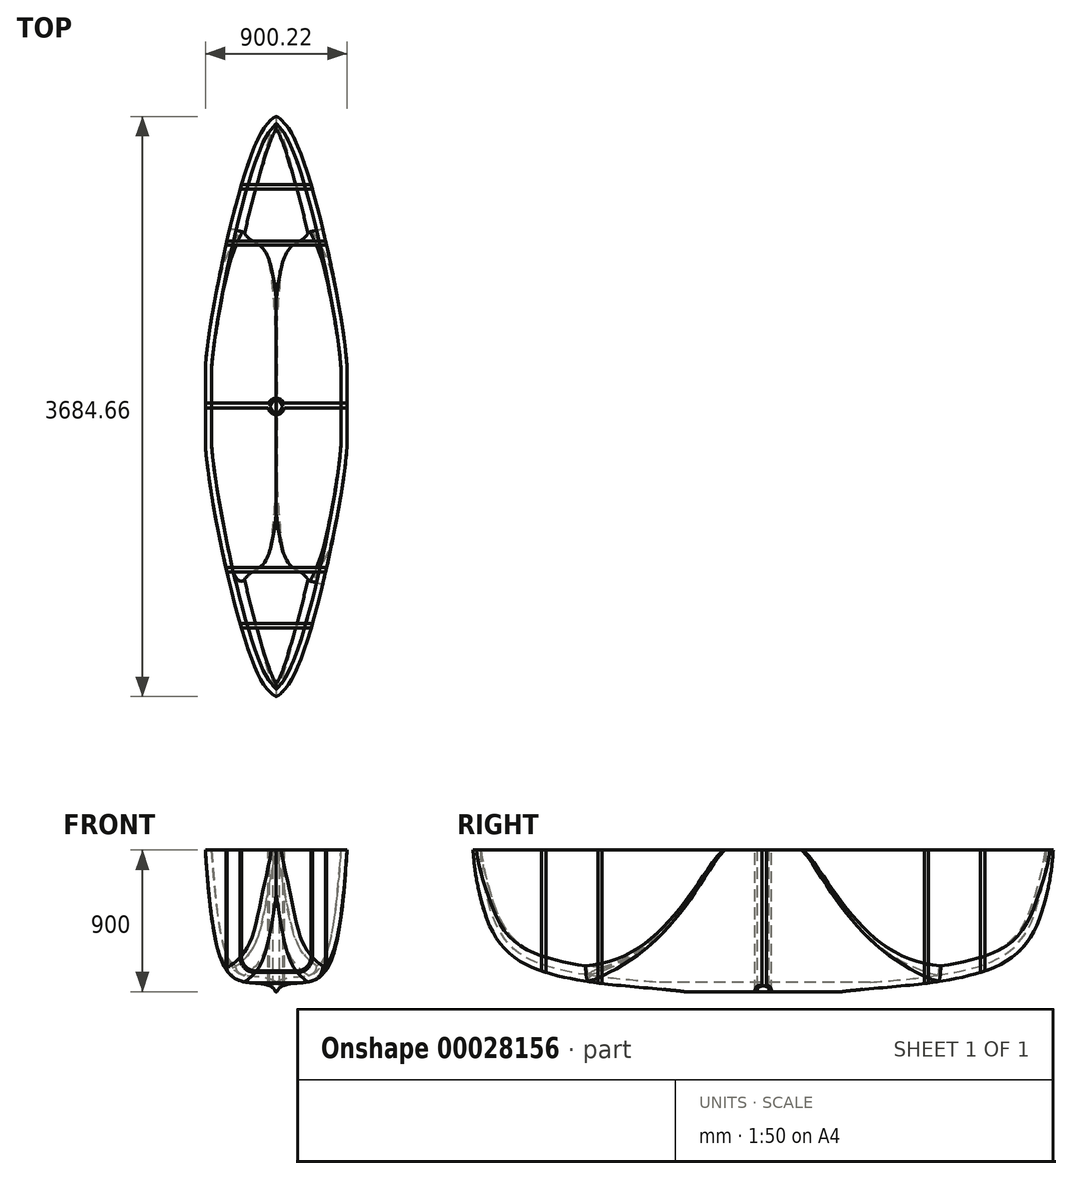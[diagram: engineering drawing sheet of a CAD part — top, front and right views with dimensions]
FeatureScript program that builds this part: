
annotation { "Feature Type Name" : "Feature", "Feature Type Description" : "" }
export const myFeature = defineFeature(function(context is Context, id is Id, definition is map)
    precondition{}
    {
        {
            var Q0;
            Q0=qCreatedBy(makeId("Front.planeOp"),FACE);
            var sketch = newSketch(context, id + "F0", { "sketchPlane" : qUnion([Q0])});
            skLineSegment(sketch, "E0.rect.bottom", {"start": v(450, -450) * mm, "end": v(-450, -450) * mm});
            skLineSegment(sketch, "E0.rect.top", {"start": v(450, 450) * mm, "end": v(-450, 450) * mm});
            skLineSegment(sketch, "E0.rect.left", {"start": v(450, -450) * mm, "end": v(450, 450) * mm});
            skLineSegment(sketch, "E0.rect.right", {"start": v(-450, -450) * mm, "end": v(-450, 450) * mm});
            skPoint(sketch, "E0.rect.middle", {"position": v(0, 0) * mm});
            skSolve(sketch);
        }
        {
            var Q0;
            Q0 = qSketchRegion(id + "F0", true);
            extrude(context, id + "F1", {"entities" : qUnion([Q0]), "endBound" : BoundingType.SYMMETRIC, "depth" : 3700 * mm});
        }
        {
            var Q0;
            Q0=makeQuery(id+"F1.opExtrude","CAP_FACE",FACE,{"disambiguationData":[OSD([sQuery(id+"F0.wireOp",EDGE,"E0.rect.bottom"),sQuery(id+"F0.wireOp",EDGE,"E0.rect.top"),sQuery(id+"F0.wireOp",EDGE,"E0.rect.left"),sQuery(id+"F0.wireOp",EDGE,"E0.rect.right")])],"isStart":false});
            var sketch = newSketch(context, id + "F2", { "sketchPlane" : qUnion([Q0])});
            skLineSegment(sketch, "E1", {"start": v(0, -450) * mm, "end": v(0, 450) * mm, "construction": true});
            skLineSegment(sketch, "E2", {"start": v(0, -450) * mm, "end": v(5, -450) * mm});
            skFitSpline(sketch, "E3", {"points": [v(5, -450) * mm, v(227.43, -381.86) * mm, v(386.95, -116.91) * mm, v(450, 450) * mm], "startDerivative": vector(294.58, 786.1) * mm, "endDerivative": vector(57.57, 897.48) * mm});
            skLineSegment(sketch, "E4.MirrorCS", {"start": v(0, -450) * mm, "end": v(-5, -450) * mm});
            skFitSpline(sketch, "E5.MirrorCS", {"points": [v(-5, -450) * mm, v(-227.43, -381.86) * mm, v(-386.95, -116.91) * mm, v(-450, 450) * mm], "startDerivative": vector(-294.58, 786.1) * mm, "endDerivative": vector(-57.57, 897.48) * mm});
            skSolve(sketch);
        }
        {
            var Q0;
            Q0=makeQuery(id+"F1.opExtrude","SWEPT_FACE",FACE,{"disambiguationData":[OSD([sQuery(id+"F0.wireOp",EDGE,"E0.rect.right")])]});
            var sketch = newSketch(context, id + "F3", { "sketchPlane" : qUnion([Q0])});
            skLineSegment(sketch, "E6", {"start": v(0, -450) * mm, "end": v(500, -450) * mm});
            skLineSegment(sketch, "E7", {"start": v(0, -450) * mm, "end": v(0, 450) * mm, "construction": true});
            skFitSpline(sketch, "E8", {"points": [v(500, -450) * mm, v(1533.69, -262.8) * mm, v(1795.23, 146) * mm, v(1850, 450) * mm], "startDerivative": vector(1866.26, 245.74) * mm, "endDerivative": vector(116.04, 1077.86) * mm});
            skLineSegment(sketch, "E9.MirrorCS", {"start": v(0, -450) * mm, "end": v(-500, -450) * mm});
            skFitSpline(sketch, "E10.MirrorCS", {"points": [v(-500, -450) * mm, v(-1533.69, -262.8) * mm, v(-1795.23, 146) * mm, v(-1850, 450) * mm], "startDerivative": vector(-1866.26, 245.74) * mm, "endDerivative": vector(-116.04, 1077.86) * mm});
            skSolve(sketch);
        }
        {
            var Q0;
            {var subQ2=sQuery(id+"F3.wireOp",EDGE,"E10.MirrorCS");Q0=makeQuery(id+"F3.imprint","IMPRINT",FACE,{"disambiguationData":[TD([[makeQuery(id+"F3.imprint","IMPRINT",EDGE,{"derivedFrom":subQ2}),1.0]])]});}
            var Q1;
            {var subQ2=sQuery(id+"F3.wireOp",EDGE,"E8");Q1=makeQuery(id+"F3.imprint","IMPRINT",FACE,{"disambiguationData":[TD([[makeQuery(id+"F3.imprint","IMPRINT",EDGE,{"derivedFrom":subQ2}),-1.0]])]});}
            extrude(context, id + "F4", {"entities" : qUnion([Q0, Q1]), "operationType" : NewBodyOperationType.REMOVE, "endBound" : BoundingType.THROUGH_ALL, "oppositeDirection" : true, "depth" : 25 * mm});
        }
        {
            var Q0;
            {var subQ1=sQuery(id+"F2.wireOp",EDGE,"E3");Q0=makeQuery(id+"F2.imprint","IMPRINT",FACE,{"disambiguationData":[TD([[makeQuery(id+"F2.imprint","IMPRINT",EDGE,{"derivedFrom":subQ1}),-1.0]])]});}
            var Q1;
            {var subQ1=sQuery(id+"F2.wireOp",EDGE,"E5.MirrorCS");Q1=makeQuery(id+"F2.imprint","IMPRINT",FACE,{"disambiguationData":[TD([[makeQuery(id+"F2.imprint","IMPRINT",EDGE,{"derivedFrom":subQ1}),1.0]])]});}
            extrude(context, id + "F5", {"entities" : qUnion([Q0, Q1]), "operationType" : NewBodyOperationType.REMOVE, "endBound" : BoundingType.THROUGH_ALL, "oppositeDirection" : true, "depth" : 25 * mm});
        }
        {
            var Q0;
            Q0=makeQuery(id+"F1.opExtrude","SWEPT_FACE",FACE,{"disambiguationData":[OSD([sQuery(id+"F0.wireOp",EDGE,"E0.rect.top")])]});
            var sketch = newSketch(context, id + "F6", { "sketchPlane" : qUnion([Q0])});
            skLineSegment(sketch, "E11", {"start": v(-450, 0) * mm, "end": v(450, 0) * mm, "construction": true});
            skLineSegment(sketch, "E12", {"start": v(-450, 0) * mm, "end": v(-450, 250) * mm});
            skLineSegment(sketch, "E13", {"start": v(0, 1850) * mm, "end": v(0, -1850) * mm, "construction": true});
            skFitSpline(sketch, "E14", {"points": [v(-450, 250) * mm, v(-293.35, 1137.47) * mm, v(-112.56, 1707.62) * mm, v(0, 1850) * mm], "startDerivative": vector(77.55, 1314.78) * mm, "endDerivative": vector(838.8, 705.86) * mm});
            skFitSpline(sketch, "E15.MirrorCS", {"points": [v(-450, -250) * mm, v(-293.35, -1137.47) * mm, v(-112.56, -1707.62) * mm, v(0, -1850) * mm], "startDerivative": vector(77.55, -1314.78) * mm, "endDerivative": vector(838.8, -705.86) * mm});
            skLineSegment(sketch, "E16.MirrorCS", {"start": v(-450, 0) * mm, "end": v(-450, -250) * mm});
            skFitSpline(sketch, "E17.MirrorCS", {"points": [v(450, 250) * mm, v(293.35, 1137.47) * mm, v(112.56, 1707.62) * mm, v(0, 1850) * mm], "startDerivative": vector(-77.55, 1314.78) * mm, "endDerivative": vector(-838.8, 705.86) * mm});
            skLineSegment(sketch, "E18.MirrorCS", {"start": v(450, 0) * mm, "end": v(450, 250) * mm});
            skLineSegment(sketch, "E19.MirrorCS", {"start": v(450, 0) * mm, "end": v(450, -250) * mm});
            skFitSpline(sketch, "E20.MirrorCS", {"points": [v(450, -250) * mm, v(293.35, -1137.47) * mm, v(112.56, -1707.62) * mm, v(0, -1850) * mm], "startDerivative": vector(-77.55, -1314.78) * mm, "endDerivative": vector(-838.8, -705.86) * mm});
            skSolve(sketch);
        }
        {
            var Q0;
            {var subQ3=sQuery(id+"F6.wireOp",EDGE,"E14");Q0=makeQuery(id+"F6.imprint","IMPRINT",FACE,{"disambiguationData":[TD([[makeQuery(id+"F6.imprint","IMPRINT",EDGE,{"derivedFrom":subQ3}),1.0]])]});}
            var Q1;
            {var subQ3=sQuery(id+"F6.wireOp",EDGE,"E17.MirrorCS");Q1=makeQuery(id+"F6.imprint","IMPRINT",FACE,{"disambiguationData":[TD([[makeQuery(id+"F6.imprint","IMPRINT",EDGE,{"derivedFrom":subQ3}),-1.0]])]});}
            var Q2;
            {var subQ3=sQuery(id+"F6.wireOp",EDGE,"E20.MirrorCS");Q2=makeQuery(id+"F6.imprint","IMPRINT",FACE,{"disambiguationData":[TD([[makeQuery(id+"F6.imprint","IMPRINT",EDGE,{"derivedFrom":subQ3}),1.0]])]});}
            var Q3;
            {var subQ3=sQuery(id+"F6.wireOp",EDGE,"E15.MirrorCS");Q3=makeQuery(id+"F6.imprint","IMPRINT",FACE,{"disambiguationData":[TD([[makeQuery(id+"F6.imprint","IMPRINT",EDGE,{"derivedFrom":subQ3}),-1.0]])]});}
            extrude(context, id + "F7", {"entities" : qUnion([Q0, Q1, Q2, Q3]), "operationType" : NewBodyOperationType.REMOVE, "endBound" : BoundingType.THROUGH_ALL, "oppositeDirection" : true, "depth" : 25 * mm});
        }
        {
            var Q0;
            Q0=makeQuery(id+"F7.boolean.opBoolean","INTERSECT",EDGE,{"derivedFrom":[makeQuery(id+"F5.boolean.opBoolean","COPY",FACE,{"derivedFrom":makeQuery(id+"F5.opExtrude","SWEPT_FACE",FACE,{"disambiguationData":[OSD([sQuery(id+"F2.wireOp",EDGE,"E5.MirrorCS")])]})}),makeQuery(id+"F7.opExtrude","SWEPT_FACE",FACE,{"disambiguationData":[OSD([sQuery(id+"F6.wireOp",EDGE,"E14")])]})]});
            var Q1;
            Q1=makeQuery(id+"F7.boolean.opBoolean","INTERSECT",EDGE,{"derivedFrom":[makeQuery(id+"F4.boolean.opBoolean","COPY",FACE,{"derivedFrom":makeQuery(id+"F4.opExtrude","SWEPT_FACE",FACE,{"disambiguationData":[OSD([sQuery(id+"F3.wireOp",EDGE,"E10.MirrorCS")])]})}),makeQuery(id+"F7.opExtrude","SWEPT_FACE",FACE,{"disambiguationData":[OSD([sQuery(id+"F6.wireOp",EDGE,"E14")])]})]});
            var Q2;
            Q2=makeQuery(id+"F7.boolean.opBoolean","INTERSECT",EDGE,{"derivedFrom":[makeQuery(id+"F4.boolean.opBoolean","COPY",FACE,{"derivedFrom":makeQuery(id+"F4.opExtrude","SWEPT_FACE",FACE,{"disambiguationData":[OSD([sQuery(id+"F3.wireOp",EDGE,"E8")])]})}),makeQuery(id+"F7.opExtrude","SWEPT_FACE",FACE,{"disambiguationData":[OSD([sQuery(id+"F6.wireOp",EDGE,"E15.MirrorCS")])]})]});
            var Q3;
            Q3=makeQuery(id+"F7.boolean.opBoolean","INTERSECT",EDGE,{"derivedFrom":[makeQuery(id+"F4.boolean.opBoolean","COPY",FACE,{"derivedFrom":makeQuery(id+"F4.opExtrude","SWEPT_FACE",FACE,{"disambiguationData":[OSD([sQuery(id+"F3.wireOp",EDGE,"E8")])]})}),makeQuery(id+"F7.opExtrude","SWEPT_FACE",FACE,{"disambiguationData":[OSD([sQuery(id+"F6.wireOp",EDGE,"E20.MirrorCS")])]})]});
            var Q4;
            Q4=makeQuery(id+"F7.boolean.opBoolean","INTERSECT",EDGE,{"derivedFrom":[makeQuery(id+"F5.boolean.opBoolean","COPY",FACE,{"derivedFrom":makeQuery(id+"F5.opExtrude","SWEPT_FACE",FACE,{"disambiguationData":[OSD([sQuery(id+"F2.wireOp",EDGE,"E3")])]})}),makeQuery(id+"F7.opExtrude","SWEPT_FACE",FACE,{"disambiguationData":[OSD([sQuery(id+"F6.wireOp",EDGE,"E20.MirrorCS")])]})]});
            var Q5;
            Q5=makeQuery(id+"F7.boolean.opBoolean","INTERSECT",EDGE,{"derivedFrom":[makeQuery(id+"F5.boolean.opBoolean","COPY",FACE,{"derivedFrom":makeQuery(id+"F5.opExtrude","SWEPT_FACE",FACE,{"disambiguationData":[OSD([sQuery(id+"F2.wireOp",EDGE,"E3")])]})}),makeQuery(id+"F7.opExtrude","SWEPT_FACE",FACE,{"disambiguationData":[OSD([sQuery(id+"F6.wireOp",EDGE,"E17.MirrorCS")])]})]});
            var Q6;
            Q6=makeQuery(id+"F7.boolean.opBoolean","INTERSECT",EDGE,{"derivedFrom":[makeQuery(id+"F4.boolean.opBoolean","COPY",FACE,{"derivedFrom":makeQuery(id+"F4.opExtrude","SWEPT_FACE",FACE,{"disambiguationData":[OSD([sQuery(id+"F3.wireOp",EDGE,"E10.MirrorCS")])]})}),makeQuery(id+"F7.opExtrude","SWEPT_FACE",FACE,{"disambiguationData":[OSD([sQuery(id+"F6.wireOp",EDGE,"E17.MirrorCS")])]})]});
            fillet(context, id + "F8", {"entities" : qUnion([Q0, Q1, Q2, Q3, Q4, Q5, Q6]), "radius" : 100 * mm, "tangentPropagation" : true, "allowEdgeOverflow" : false});
        }
        {
            var Q0;
            Q0=makeQuery(id+"F1.opExtrude","SWEPT_FACE",FACE,{"disambiguationData":[OSD([sQuery(id+"F0.wireOp",EDGE,"E0.rect.top")])]});
            var sketch = newSketch(context, id + "F9", { "sketchPlane" : qUnion([Q0])});
            skCircle(sketch, "E21.cCircle", {"center": v(0, 0) * mm, "radius": 43.3 * mm, "construction": true});
            skLineSegment(sketch, "E21.0", {"start": v(21.65, -37.5) * mm, "end": v(-21.65, -37.5) * mm});
            skLineSegment(sketch, "E21.1", {"start": v(-21.65, -37.5) * mm, "end": v(-43.3, 0) * mm});
            skLineSegment(sketch, "E21.2", {"start": v(-43.3, 0) * mm, "end": v(-21.65, 37.5) * mm});
            skLineSegment(sketch, "E21.3", {"start": v(-21.65, 37.5) * mm, "end": v(21.65, 37.5) * mm});
            skLineSegment(sketch, "E21.4", {"start": v(21.65, 37.5) * mm, "end": v(43.3, 0) * mm});
            skLineSegment(sketch, "E21.5", {"start": v(43.3, 0) * mm, "end": v(21.65, -37.5) * mm});
            skCircle(sketch, "E22", {"center": v(0, 0) * mm, "radius": 52.5 * mm});
            skLineSegment(sketch, "E23", {"start": v(-48.16, 20.9) * mm, "end": v(-450, 20.9) * mm});
            skLineSegment(sketch, "E24", {"start": v(-450, 20.9) * mm, "end": v(-450, -9.1) * mm});
            skLineSegment(sketch, "E25", {"start": v(-450, -9.1) * mm, "end": v(-51.7, -9.1) * mm});
            skLineSegment(sketch, "E26", {"start": v(48.16, 20.9) * mm, "end": v(450, 20.9) * mm});
            skLineSegment(sketch, "E27", {"start": v(51.7, -9.1) * mm, "end": v(450, -9.1) * mm});
            skLineSegment(sketch, "E28", {"start": v(0, 0) * mm, "end": v(450, 0) * mm, "construction": true});
            skLineSegment(sketch, "E29", {"start": v(0, 0) * mm, "end": v(-450, 0) * mm, "construction": true});
            skLineSegment(sketch, "E30", {"start": v(-313.93, 1050.18) * mm, "end": v(313.93, 1050.18) * mm});
            skLineSegment(sketch, "E31", {"start": v(313.93, 1050.18) * mm, "end": v(319.82, 1024.35) * mm});
            skLineSegment(sketch, "E32", {"start": v(319.82, 1024.35) * mm, "end": v(-319.82, 1024.35) * mm});
            skLineSegment(sketch, "E33.MirrorCS", {"start": v(319.82, -1024.35) * mm, "end": v(-319.82, -1024.35) * mm});
            skLineSegment(sketch, "E34.MirrorCS", {"start": v(-313.93, -1050.18) * mm, "end": v(313.93, -1050.18) * mm});
            skLineSegment(sketch, "E35", {"start": v(-221.23, 1407.5) * mm, "end": v(221.23, 1407.5) * mm});
            skLineSegment(sketch, "E36", {"start": v(221.23, 1407.5) * mm, "end": v(229.37, 1379.73) * mm});
            skLineSegment(sketch, "E37", {"start": v(229.37, 1379.73) * mm, "end": v(-229.37, 1379.73) * mm});
            skLineSegment(sketch, "E38.MirrorCS", {"start": v(229.37, -1379.73) * mm, "end": v(-229.37, -1379.73) * mm});
            skLineSegment(sketch, "E39.MirrorCS", {"start": v(-221.23, -1407.5) * mm, "end": v(221.23, -1407.5) * mm});
            skSolve(sketch);
        }
        {
            var Q0;
            Q0=makeQuery(id+"F9.imprint","IMPRINT",FACE,{"disambiguationData":[TD([[makeQuery(id+"F9.imprint","IMPRINT",EDGE,{"derivedFrom":sQuery(id+"F9.wireOp",EDGE,"E21.0")}),1.0]])]});
            var Q1;
            {var subQ4=sQuery(id+"F9.wireOp",EDGE,"E26");Q1=makeQuery(id+"F9.imprint","IMPRINT",FACE,{"disambiguationData":[TD([[makeQuery(id+"F9.imprint","IMPRINT",EDGE,{"derivedFrom":subQ4}),-1.0]])]});}
            var Q2;
            {var subQ1=sQuery(id+"F9.wireOp",EDGE,"E23");Q2=makeQuery(id+"F9.imprint","IMPRINT",FACE,{"disambiguationData":[TD([[makeQuery(id+"F9.imprint","IMPRINT",EDGE,{"derivedFrom":subQ1}),1.0]])]});}
            var Q3;
            {var subQ2=sQuery(id+"F9.wireOp",EDGE,"E33.MirrorCS");Q3=makeQuery(id+"F9.imprint","IMPRINT",FACE,{"disambiguationData":[TD([[makeQuery(id+"F9.imprint","IMPRINT",EDGE,{"derivedFrom":subQ2}),1.0]])]});}
            var Q4;
            {var subQ2=sQuery(id+"F9.wireOp",EDGE,"E30");Q4=makeQuery(id+"F9.imprint","IMPRINT",FACE,{"disambiguationData":[TD([[makeQuery(id+"F9.imprint","IMPRINT",EDGE,{"derivedFrom":subQ2}),-1.0]])]});}
            var Q5;
            {var subQ2=sQuery(id+"F9.wireOp",EDGE,"E35");Q5=makeQuery(id+"F9.imprint","IMPRINT",FACE,{"disambiguationData":[TD([[makeQuery(id+"F9.imprint","IMPRINT",EDGE,{"derivedFrom":subQ2}),-1.0]])]});}
            var Q6;
            {var subQ2=sQuery(id+"F9.wireOp",EDGE,"E38.MirrorCS");Q6=makeQuery(id+"F9.imprint","IMPRINT",FACE,{"disambiguationData":[TD([[makeQuery(id+"F9.imprint","IMPRINT",EDGE,{"derivedFrom":subQ2}),1.0]])]});}
            extrude(context, id + "F10", {"entities" : qUnion([Q0, Q1, Q2, Q3, Q4, Q5, Q6]), "endBound" : BoundingType.UP_TO_NEXT, "oppositeDirection" : true, "depth" : 25 * mm});
        }
        {
            var Q0;
            Q0=makeQuery(id+"F1.opExtrude","SWEPT_FACE",FACE,{"disambiguationData":[OSD([sQuery(id+"F0.wireOp",EDGE,"E0.rect.top")])]});
            shell(context, id + "F11", {"entities" : qUnion([Q0]), "thickness" : 40 * mm});
        }
    });
